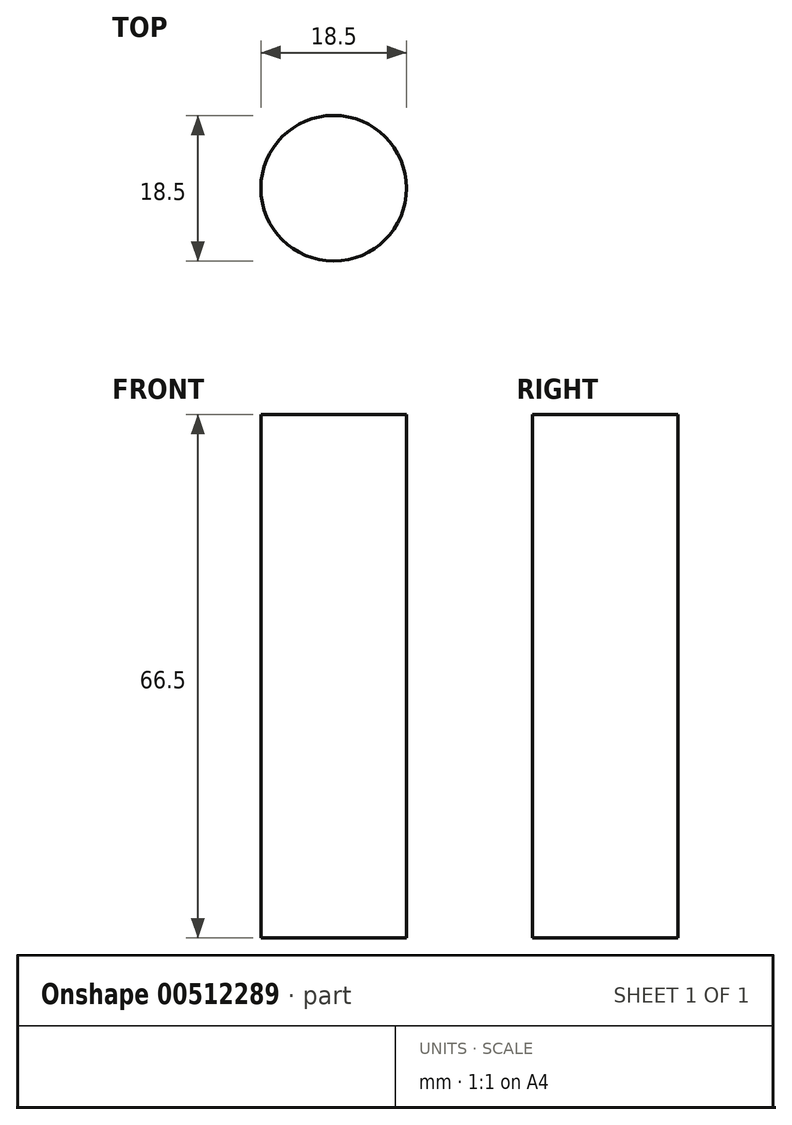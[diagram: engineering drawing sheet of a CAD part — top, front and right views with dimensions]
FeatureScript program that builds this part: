
annotation { "Feature Type Name" : "Feature", "Feature Type Description" : "" }
export const myFeature = defineFeature(function(context is Context, id is Id, definition is map)
    precondition{}
    {
        {
            var Q0;
            Q0=qCreatedBy(makeId("Top.planeOp"),FACE);
            var sketch = newSketch(context, id + "F0", { "sketchPlane" : qUnion([Q0])});
            skCircle(sketch, "E0", {"center": v(0, 0) * mm, "radius": 9.25 * mm});
            skSolve(sketch);
        }
        {
            var Q0;
            Q0 = qSketchRegion(id + "F0", true);
            extrude(context, id + "F1", {"entities" : qUnion([Q0]), "oppositeDirection" : true, "depth" : 66.5 * mm, "offsetDistance" : 25 * mm});
        }
    });
